# Revit family: Sunshade-Corner-Kawneer-Curtain_Wall-Inside_135
name_source: partatom
category: Specialty Equipment
revit_build: Autodesk Revit 2015 (Build: 20140905_0730(x64)
units: mm (PartAtom-declared; Revit-internal decimal feet)

## types (1)
- 36"-Circular-Square
    Angle Offset = 0' - 2"
    Blade 1 Location = 0' - 0"
    Blade 2 Location = 0' - 0"
    Blade 3 Location = 0' - 0"
    Blade 4 Location = 0' - 0"
    Blade 5 Location = 0' - 0"
    Blade 6 Location = 0' - 0"
    Blade Cut Angle = 67.50°
    Blade Distance = 0' - 5"
    Blade Type = Blade-Kawneer-135_Angle_Cut-Circular : Versoleil
    Bottom Fascia Offset = 1' - 2"
    CTRL Angle = 135.00°
    CTRL Fascia Location = 0' - 0"
    CTRL Length of Blade = 4' - 2 1/32"
    CTRL Outrigger Angle = 112.50°
    Default Elevation = 4' - 0"
    Description = Rounded Outrigger, Bullnose Fascias
    Distance Blade 1 and 2 = 0' - 0"
    Distance Blade 2 and 3 = 0' - 0"
    Distance Blade 3 and 4 = 0' - 0"
    Distance Blade 4 and 5 = 0' - 0"
    Distance Blade 5 and 6 = 0' - 0"
    Fascia Type = Fascia-Kawneer-Inside_135_Angle_Cut-Rectangular : Versoleil
    Finish = Aluminum - Kawneer - Clear
    Has 5th Blade = Yes
    Has 6th Blade = No
    Height of Blade 1 = 0' - 5"
    Height of Bottom Fascia = 3' - 0"
    Length = 3' - 0"
    Manufacturer = Kawneer
    Model = Sunshade Inside 135 Degree Corner
    Outrigger Type = Outrigger-Kawneer-Angle-Square : 5"
    Product Documentation Link = http://www.kawneer.com
    Product Page URL = http://www.kawneer.com
    Product data url = https://bimobject.com
    Right Fascia Offset = 1' - 3 1/2"
    Set 1 Inset = 0' - 3"
    Set 2 Inset = 0' - 0 3/4"
    URL = http://www.kawneer.com

## geometry (parser evidence)
native form markers: Sweep x44
no freeform markers — native parametric forms only
